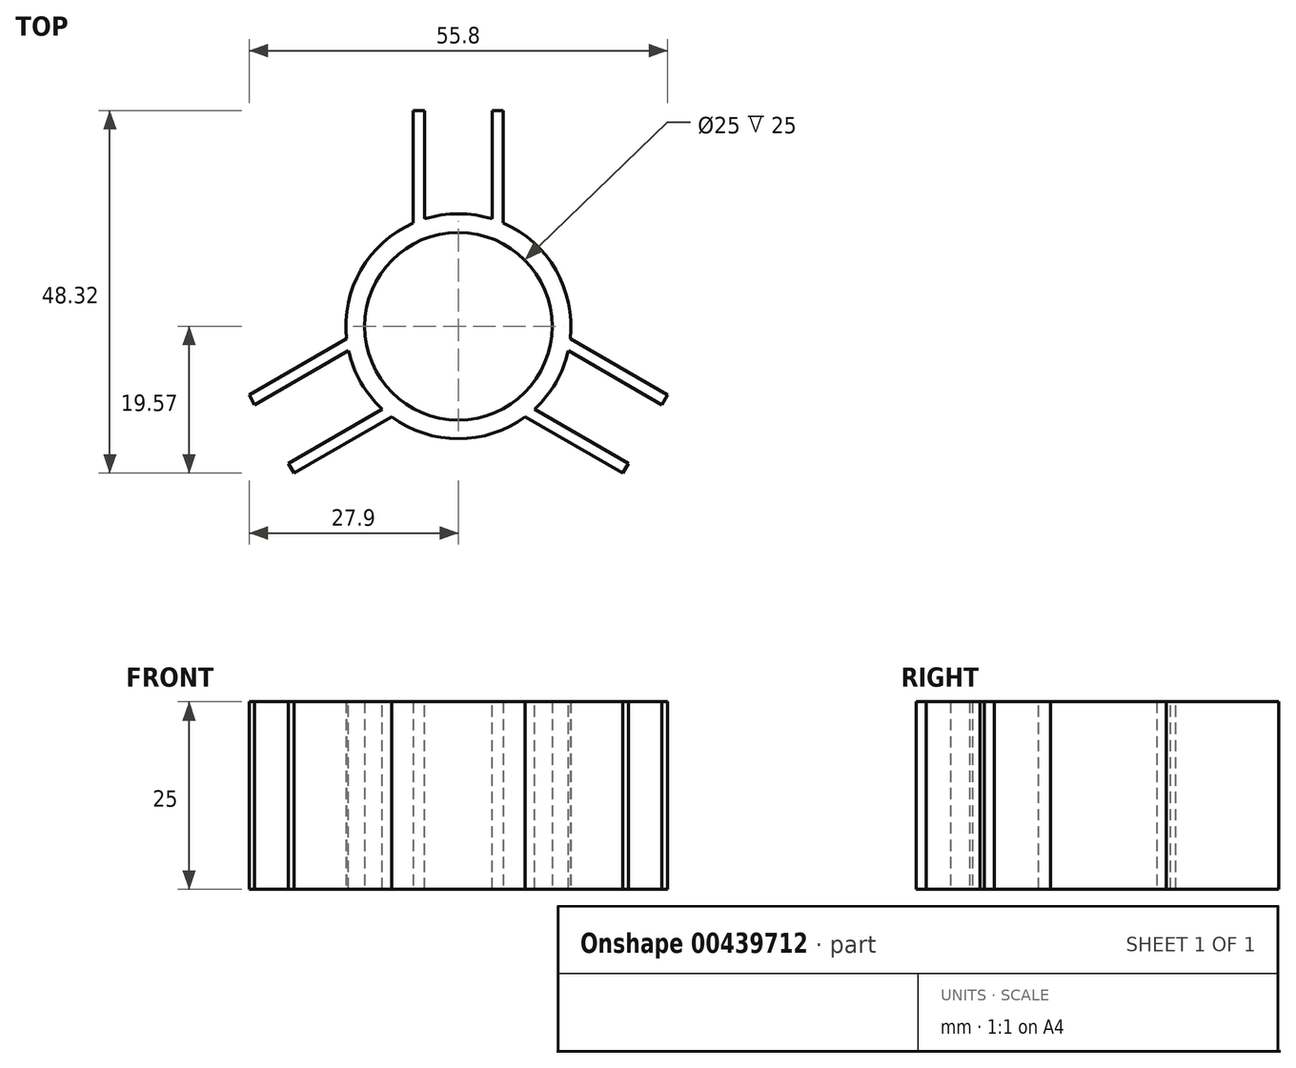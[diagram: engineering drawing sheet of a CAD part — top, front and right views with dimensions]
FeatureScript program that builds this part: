
annotation { "Feature Type Name" : "Feature", "Feature Type Description" : "" }
export const myFeature = defineFeature(function(context is Context, id is Id, definition is map)
    precondition{}
    {
        {
            var Q0;
            Q0=qCreatedBy(makeId("Top.planeOp"),FACE);
            var sketch = newSketch(context, id + "F0", { "sketchPlane" : qUnion([Q0])});
            skArc(sketch, "E0", {"start": v(-6, 13.75) * mm, "mid": v(-13, 7.5) * mm, "end": v(-14.9, -1.68) * mm});
            skCircle(sketch, "E1", {"center": v(0, 0) * mm, "radius": 12.5 * mm});
            skLineSegment(sketch, "E2", {"start": v(0, 28.75) * mm, "end": v(6, 28.75) * mm});
            skLineSegment(sketch, "E3", {"start": v(6, 28.75) * mm, "end": v(6, 13.75) * mm});
            skLineSegment(sketch, "E4", {"start": v(0, 0) * mm, "end": v(66.2, -38.22) * mm, "construction": true});
            skLineSegment(sketch, "E5", {"start": v(8.9, -12.07) * mm, "end": v(21.9, -19.57) * mm});
            skLineSegment(sketch, "E6", {"start": v(21.9, -19.57) * mm, "end": v(24.9, -14.37) * mm});
            skLineSegment(sketch, "E7", {"start": v(24.9, -14.37) * mm, "end": v(27.9, -9.18) * mm});
            skLineSegment(sketch, "E8", {"start": v(27.9, -9.18) * mm, "end": v(14.9, -1.68) * mm});
            skLineSegment(sketch, "E9.MirrorCS", {"start": v(0, 28.75) * mm, "end": v(-6, 28.75) * mm});
            skLineSegment(sketch, "E10.MirrorCS", {"start": v(-6, 28.75) * mm, "end": v(-6, 13.75) * mm});
            skLineSegment(sketch, "E11.MirrorCS", {"start": v(-27.9, -9.18) * mm, "end": v(-14.9, -1.68) * mm});
            skLineSegment(sketch, "E12.MirrorCS", {"start": v(-24.9, -14.37) * mm, "end": v(-27.9, -9.18) * mm});
            skLineSegment(sketch, "E13.MirrorCS", {"start": v(-21.9, -19.57) * mm, "end": v(-24.9, -14.37) * mm});
            skLineSegment(sketch, "E14.MirrorCS", {"start": v(-8.9, -12.07) * mm, "end": v(-21.9, -19.57) * mm});
            skArc(sketch, "E15.trimOffspring", {"start": v(14.9, -1.68) * mm, "mid": v(13, 7.5) * mm, "end": v(6, 13.75) * mm});
            skArc(sketch, "E16.trimOffspring", {"start": v(-8.9, -12.07) * mm, "mid": v(0, -15) * mm, "end": v(8.9, -12.07) * mm});
            skSolve(sketch);
        }
        {
            var Q0;
            Q0=makeQuery(id+"F0.imprint","IMPRINT",FACE,{"disambiguationData":[TD([[makeQuery(id+"F0.imprint","IMPRINT",EDGE,{"derivedFrom":sQuery(id+"F0.wireOp",EDGE,"E0")}),1.0]])]});
            extrude(context, id + "F1", {"entities" : qUnion([Q0]), "depth" : 25 * mm});
        }
        {
            var Q0;
            Q0=makeQuery(id+"F1.opExtrude","CAP_FACE",FACE,{"disambiguationData":[OSD([sQuery(id+"F0.wireOp",EDGE,"E0"),sQuery(id+"F0.wireOp",EDGE,"E1"),sQuery(id+"F0.wireOp",EDGE,"E2"),sQuery(id+"F0.wireOp",EDGE,"E3"),sQuery(id+"F0.wireOp",EDGE,"E5"),sQuery(id+"F0.wireOp",EDGE,"E6"),sQuery(id+"F0.wireOp",EDGE,"E7"),sQuery(id+"F0.wireOp",EDGE,"E8"),sQuery(id+"F0.wireOp",EDGE,"E9.MirrorCS"),sQuery(id+"F0.wireOp",EDGE,"E10.MirrorCS"),sQuery(id+"F0.wireOp",EDGE,"E11.MirrorCS"),sQuery(id+"F0.wireOp",EDGE,"E12.MirrorCS"),sQuery(id+"F0.wireOp",EDGE,"E13.MirrorCS"),sQuery(id+"F0.wireOp",EDGE,"E14.MirrorCS"),sQuery(id+"F0.wireOp",EDGE,"E15.trimOffspring"),sQuery(id+"F0.wireOp",EDGE,"E16.trimOffspring")])],"isStart":false});
            var sketch = newSketch(context, id + "F2", { "sketchPlane" : qUnion([Q0])});
            skLineSegment(sketch, "E17", {"start": v(-4.5, 28.75) * mm, "end": v(-4.5, 14.3) * mm});
            skLineSegment(sketch, "E18", {"start": v(14.64, -3.26) * mm, "end": v(27.15, -10.48) * mm});
            skLineSegment(sketch, "E19", {"start": v(10.14, -11.05) * mm, "end": v(22.65, -18.27) * mm});
            skArc(sketch, "E20", {"start": v(10.14, -11.05) * mm, "mid": v(13, -7.5) * mm, "end": v(14.64, -3.26) * mm});
            skPoint(sketch, "E21.orphan", {"position": v(8.9, -10.34) * mm});
            skLineSegment(sketch, "E22.MirrorCS", {"start": v(4.5, 28.75) * mm, "end": v(4.5, 14.3) * mm});
            skLineSegment(sketch, "E23.MirrorCS", {"start": v(-10.14, -11.05) * mm, "end": v(-22.65, -18.27) * mm});
            skLineSegment(sketch, "E24.MirrorCS", {"start": v(-14.64, -3.26) * mm, "end": v(-27.15, -10.48) * mm});
            skArc(sketch, "E25.MirrorCS", {"start": v(-10.14, -11.05) * mm, "mid": v(-13, -7.5) * mm, "end": v(-14.64, -3.26) * mm});
            skArc(sketch, "E26.trimOffspring", {"start": v(-4.5, 14.3) * mm, "mid": v(0, 15) * mm, "end": v(4.5, 14.3) * mm});
            skArc(sketch, "E27.trimOffspring", {"start": v(4.5, 14.3) * mm, "mid": v(0, 15) * mm, "end": v(-4.5, 14.3) * mm});
            skLineSegment(sketch, "E28", {"start": v(-4.5, 28.75) * mm, "end": v(4.5, 28.75) * mm});
            skLineSegment(sketch, "E29", {"start": v(27.15, -10.48) * mm, "end": v(22.65, -18.27) * mm});
            skLineSegment(sketch, "E30", {"start": v(-27.15, -10.48) * mm, "end": v(-22.65, -18.27) * mm});
            skSolve(sketch);
        }
        {
            var Q0;
            Q0 = qSketchRegion(id + "F2", true);
            extrude(context, id + "F3", {"entities" : qUnion([Q0]), "operationType" : NewBodyOperationType.REMOVE, "oppositeDirection" : true, "depth" : 25 * mm});
        }
    });
